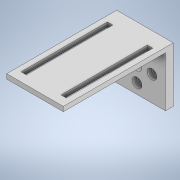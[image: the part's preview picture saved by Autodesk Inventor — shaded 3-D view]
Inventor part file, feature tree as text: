
AUTODESK INVENTOR PART (.ipt)
format: ipt  version: 2020 (Build 240168000, 168)  size: 346,112 bytes
history: native  units: in
note: dims shown in document units (in); Inventor stores cm internally (conversion verified against a paired STEP export)
features: extrude x8, sketch x7
ambient origin geometry x8: Origin, YZ Plane, XZ Plane, XY Plane, X Axis, Y Axis, Z Axis, Center Point
bodies: Solid1 (feature_tree)
feature tree (15):
  extrude  "Extrusion1"  Depth=1.2598in
  extrude  "Extrusion2"  Depth=0.1181in
  extrude  "Extrusion3"  Depth=1.5748in TaperAngle=360.0deg
  extrude  "Extrusion5"  Depth=0.1969in
  extrude  "Extrusion6"  Depth=0.0984in TaperAngle=0.0deg
  extrude  "Extrusion8"  Depth=0.3937in TaperAngle=0.0deg
  extrude  "Extrusion9"  Depth=0.1181in
  extrude  "Extrusion10"  Depth=2.7559in TaperAngle=0.0deg
  sketch  "Sketch1"  dims[d1=1.2598in d2=1.2598in]
  sketch  "Sketch2"  dims[d3=0.1969in d4=0.0in d5=0.1181in]
  sketch  "Sketch3"  dims[d6=0.374in d7=1.5748in d9=360.0deg]
  sketch  "Sketch5"  dims[d11=0.1969in d12=0.0in d13=0.2441in]
  sketch  "Sketch10"  dims[d14=1.5748in d16=360.0deg d18=0.0984in d19=0.0in]
  sketch  "Sketch11"  dims[d25=0.2362in d26=0.3937in d27=0.0in]
  sketch  "Sketch12"  dims[d32=1.2598in d33=0.1181in d34=2.7559in d35=0.0in d41=0.8661in d42=0.1378in d43=0.1378in d44=2.1654in d45=2.1654in d46=0.3937in d47=0.0in d49=0.0787in d50=0.0in d51=0.0787in d52=0.0in]
